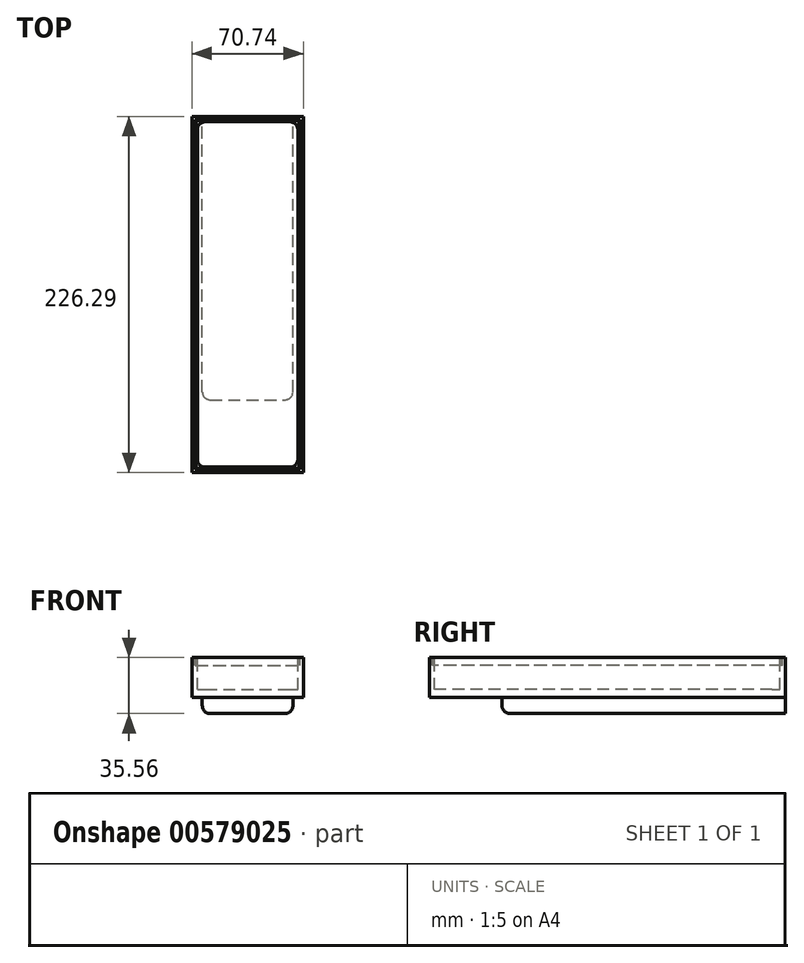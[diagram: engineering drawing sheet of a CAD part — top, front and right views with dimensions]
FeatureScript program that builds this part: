
annotation { "Feature Type Name" : "Feature", "Feature Type Description" : "" }
export const myFeature = defineFeature(function(context is Context, id is Id, definition is map)
    precondition{}
    {
        {
            var Q0;
            Q0=qCreatedBy(makeId("Top.planeOp"),FACE);
            var sketch = newSketch(context, id + "F0", { "sketchPlane" : qUnion([Q0])});
            skLineSegment(sketch, "E0.bottom", {"start": v(-58.77, 122.75) * mm, "end": v(11.97, 122.75) * mm});
            skLineSegment(sketch, "E0.top", {"start": v(-58.77, -103.54) * mm, "end": v(11.97, -103.54) * mm});
            skLineSegment(sketch, "E0.left", {"start": v(-58.77, 122.75) * mm, "end": v(-58.77, -103.54) * mm});
            skLineSegment(sketch, "E0.right", {"start": v(11.97, 122.75) * mm, "end": v(11.97, -103.54) * mm});
            skSolve(sketch);
        }
        {
            var Q0;
            Q0=makeQuery(id+"F0.imprint","IMPRINT",FACE,{"disambiguationData":[TD([[makeQuery(id+"F0.imprint","IMPRINT",EDGE,{"derivedFrom":sQuery(id+"F0.wireOp",EDGE,"E0.bottom")}),-1.0]])]});
            extrude(context, id + "F1", {"entities" : qUnion([Q0]), "depth" : 25.4 * mm, "offsetDistance" : 25.4 * mm});
        }
        {
            var Q0;
            Q0=makeQuery(id+"F1.opExtrude","CAP_FACE",FACE,{"disambiguationData":[OSD([sQuery(id+"F0.wireOp",EDGE,"E0.bottom"),sQuery(id+"F0.wireOp",EDGE,"E0.top"),sQuery(id+"F0.wireOp",EDGE,"E0.left"),sQuery(id+"F0.wireOp",EDGE,"E0.right")])],"isStart":false});
            var sketch = newSketch(context, id + "F2", { "sketchPlane" : qUnion([Q0])});
            skLineSegment(sketch, "E1.bottom", {"start": v(-55.31, 119.32) * mm, "end": v(8.52, 119.32) * mm});
            skLineSegment(sketch, "E1.top", {"start": v(-55.31, -100.1) * mm, "end": v(8.52, -100.1) * mm});
            skLineSegment(sketch, "E1.left", {"start": v(-55.31, 119.32) * mm, "end": v(-55.31, -100.1) * mm});
            skLineSegment(sketch, "E1.right", {"start": v(8.52, 119.32) * mm, "end": v(8.52, -100.1) * mm});
            skSolve(sketch);
        }
        {
            var Q0;
            Q0 = qSketchRegion(id + "F2", true);
            extrude(context, id + "F3", {"entities" : qUnion([Q0]), "operationType" : NewBodyOperationType.REMOVE, "oppositeDirection" : true, "depth" : 20.32 * mm, "offsetDistance" : 25.4 * mm});
        }
        {
            var Q0;
            Q0=makeQuery(id+"F1.opExtrude","CAP_FACE",FACE,{"disambiguationData":[OSD([sQuery(id+"F0.wireOp",EDGE,"E0.bottom"),sQuery(id+"F0.wireOp",EDGE,"E0.top"),sQuery(id+"F0.wireOp",EDGE,"E0.left"),sQuery(id+"F0.wireOp",EDGE,"E0.right")])],"isStart":true});
            var sketch = newSketch(context, id + "F4", { "sketchPlane" : qUnion([Q0])});
            skLineSegment(sketch, "E2.bottom", {"start": v(-52.19, 57.31) * mm, "end": v(5.4, 57.31) * mm});
            skLineSegment(sketch, "E2.top", {"start": v(-52.19, -122.75) * mm, "end": v(5.4, -122.75) * mm});
            skLineSegment(sketch, "E2.left", {"start": v(-52.19, 57.31) * mm, "end": v(-52.19, -122.75) * mm});
            skLineSegment(sketch, "E2.right", {"start": v(5.4, 57.31) * mm, "end": v(5.4, -122.75) * mm});
            skSolve(sketch);
        }
        {
            var Q0;
            Q0 = qSketchRegion(id + "F4", true);
            extrude(context, id + "F5", {"entities" : qUnion([Q0]), "operationType" : NewBodyOperationType.ADD, "depth" : 10.16 * mm, "offsetDistance" : 25.4 * mm});
        }
        {
            var Q0;
            Q0=makeQuery(id+"F5.opExtrude","CAP_EDGE",EDGE,{"disambiguationData":[OSD([sQuery(id+"F4.wireOp",EDGE,"E2.bottom")])],"isStart":false});
            var Q1;
            Q1=makeQuery(id+"F5.opExtrude","CAP_EDGE",EDGE,{"disambiguationData":[OSD([sQuery(id+"F4.wireOp",EDGE,"E2.right")])],"isStart":false});
            var Q2;
            Q2=makeQuery(id+"F5.opExtrude","CAP_EDGE",EDGE,{"disambiguationData":[OSD([sQuery(id+"F4.wireOp",EDGE,"E2.left")])],"isStart":false});
            var Q3;
            Q3=makeQuery(id+"F5.opExtrude","SWEPT_EDGE",EDGE,{"disambiguationData":[OSD([sQuery(id+"F4.wireOp",EDGE,"E2.bottom"),sQuery(id+"F4.wireOp",EDGE,"E2.right")])]});
            var Q4;
            Q4=makeQuery(id+"F5.opExtrude","SWEPT_EDGE",EDGE,{"disambiguationData":[OSD([sQuery(id+"F4.wireOp",EDGE,"E2.bottom"),sQuery(id+"F4.wireOp",EDGE,"E2.left")])]});
            var Q5;
            Q5=makeQuery(id+"F3.boolean.opBoolean","COPY",EDGE,{"derivedFrom":makeQuery(id+"F3.opExtrude","SWEPT_EDGE",EDGE,{"disambiguationData":[OSD([sQuery(id+"F2.wireOp",EDGE,"E1.top"),sQuery(id+"F2.wireOp",EDGE,"E1.right")])]})});
            var Q6;
            Q6=makeQuery(id+"F3.boolean.opBoolean","COPY",EDGE,{"derivedFrom":makeQuery(id+"F3.opExtrude","SWEPT_EDGE",EDGE,{"disambiguationData":[OSD([sQuery(id+"F2.wireOp",EDGE,"E1.bottom"),sQuery(id+"F2.wireOp",EDGE,"E1.right")])]})});
            var Q7;
            Q7=makeQuery(id+"F3.boolean.opBoolean","COPY",EDGE,{"derivedFrom":makeQuery(id+"F3.opExtrude","SWEPT_EDGE",EDGE,{"disambiguationData":[OSD([sQuery(id+"F2.wireOp",EDGE,"E1.bottom"),sQuery(id+"F2.wireOp",EDGE,"E1.left")])]})});
            var Q8;
            Q8=makeQuery(id+"F3.boolean.opBoolean","COPY",EDGE,{"derivedFrom":makeQuery(id+"F3.opExtrude","SWEPT_EDGE",EDGE,{"disambiguationData":[OSD([sQuery(id+"F2.wireOp",EDGE,"E1.top"),sQuery(id+"F2.wireOp",EDGE,"E1.left")])]})});
            fillet(context, id + "F6", {"entities" : qUnion([Q0, Q1, Q2, Q3, Q4, Q5, Q6, Q7, Q8]), "radius" : 5.08 * mm, "tangentPropagation" : true, "allowEdgeOverflow" : false});
        }
        {
            var Q0;
            Q0=makeQuery(id+"F1.opExtrude","CAP_FACE",FACE,{"disambiguationData":[OSD([sQuery(id+"F0.wireOp",EDGE,"E0.bottom"),sQuery(id+"F0.wireOp",EDGE,"E0.top"),sQuery(id+"F0.wireOp",EDGE,"E0.left"),sQuery(id+"F0.wireOp",EDGE,"E0.right")])],"isStart":false});
            var sketch = newSketch(context, id + "F7", { "sketchPlane" : qUnion([Q0])});
            skLineSegment(sketch, "E3.bottom", {"start": v(-56.84, 120.84) * mm, "end": v(10.04, 120.84) * mm});
            skLineSegment(sketch, "E3.top", {"start": v(-56.84, -101.63) * mm, "end": v(10.04, -101.63) * mm});
            skLineSegment(sketch, "E3.left", {"start": v(-56.84, 120.84) * mm, "end": v(-56.84, -101.63) * mm});
            skLineSegment(sketch, "E3.right", {"start": v(10.04, 120.84) * mm, "end": v(10.04, -101.63) * mm});
            skLineSegment(sketch, "E4.bottom", {"start": v(-56.08, 120.08) * mm, "end": v(9.28, 120.08) * mm});
            skLineSegment(sketch, "E4.top", {"start": v(-56.08, -100.87) * mm, "end": v(9.28, -100.87) * mm});
            skLineSegment(sketch, "E4.left", {"start": v(-56.08, 120.08) * mm, "end": v(-56.08, -100.87) * mm});
            skLineSegment(sketch, "E4.right", {"start": v(9.28, 120.08) * mm, "end": v(9.28, -100.87) * mm});
            skSolve(sketch);
        }
        {
            var Q0;
            Q0 = qSketchRegion(id + "F7", true);
            extrude(context, id + "F8", {"entities" : qUnion([Q0]), "operationType" : NewBodyOperationType.REMOVE, "oppositeDirection" : true, "depth" : 5 * mm, "offsetDistance" : 25.4 * mm});
        }
    });
